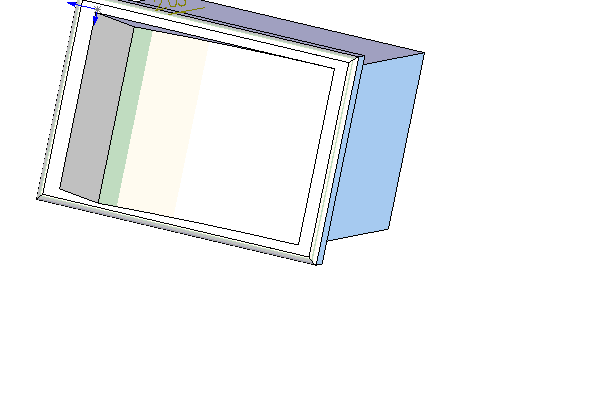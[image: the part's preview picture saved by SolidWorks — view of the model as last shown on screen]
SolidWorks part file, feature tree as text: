
SOLIDWORKS PART (.sldprt)
format: sldprt  version: not decoded by parser v0  size: 121,344 bytes
history: native  units: mm
features: sketch x3, extrude x3, material x1, fillet x1 + 1 further entry (+12 scaffold rows collapsed)
feature tree (21):
  "Annotations"  RD1=2.03mm
  scaffold x12  (default folders/planes/origin — collapsed)
  material  "Material <not specified>"
  sketch  "Sketch1"  dims[D1=12.7mm D2=18.54mm]
  extrude  "Extrude1"  Depth=20.14mm
  sketch  "Sketch2"  dims[D1=20.83mm D2=15.0mm D3=1.15mm D4=1.1425mm]
  extrude  "Extrude2"  Depth=2.03mm
  fillet  "Fillet1"  Radius=0.5mm
  sketch  "Sketch3"
  extrude  "Extrude3"  Depth=12.7mm
decode coverage: 6 of 7 modeling features carry decoded parameters; 1 rows unclassified (native names shown)
note: suppression state not decoded; provenance and decode notes live in map.json
